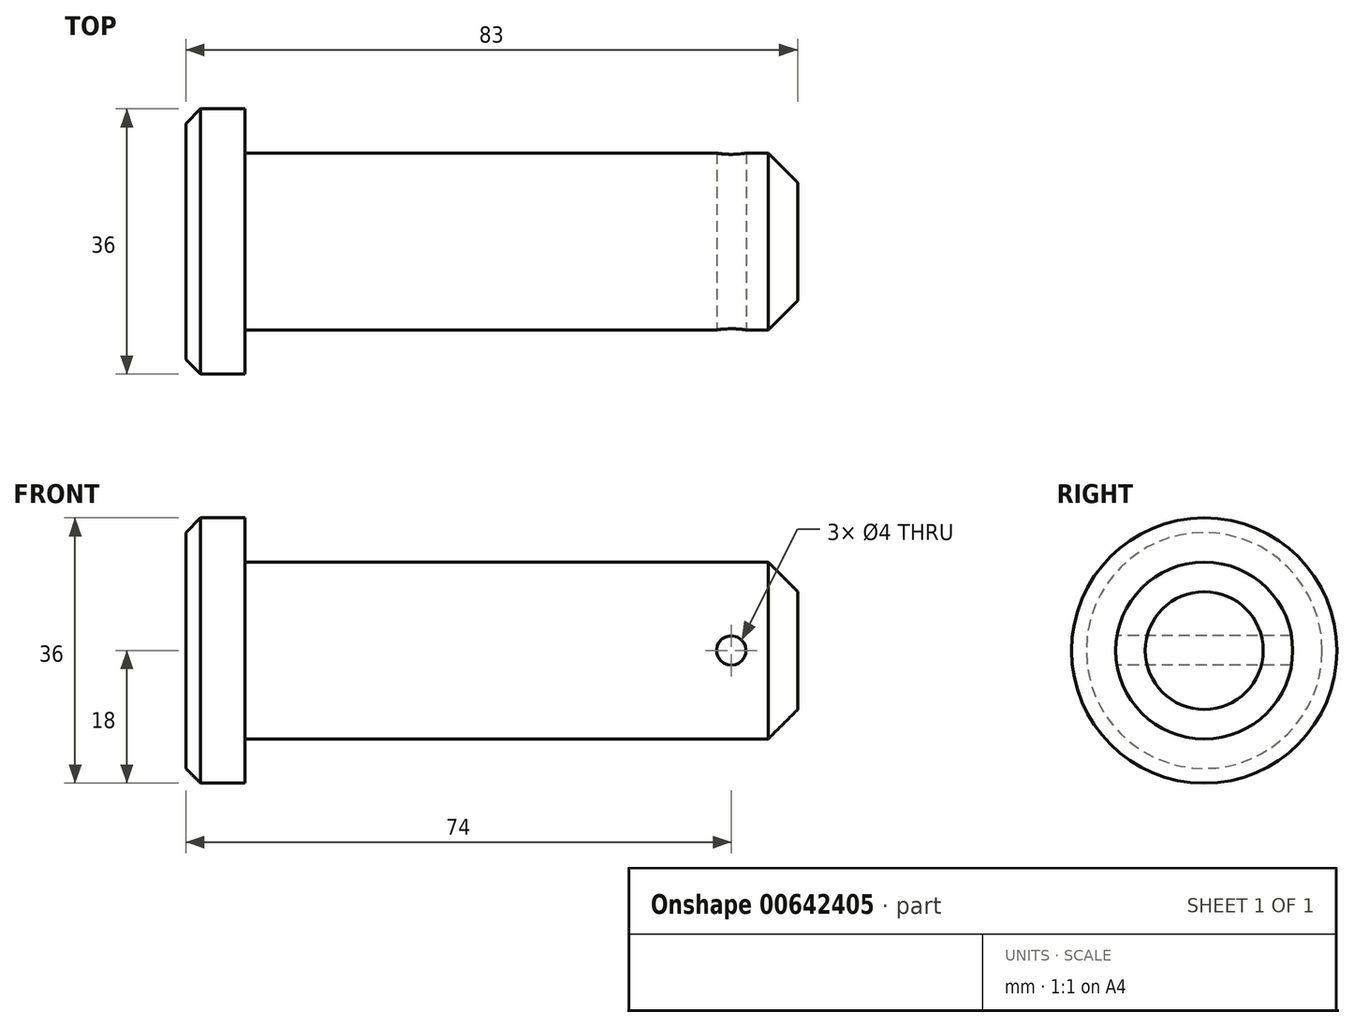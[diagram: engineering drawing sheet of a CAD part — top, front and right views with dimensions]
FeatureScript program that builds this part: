
annotation { "Feature Type Name" : "Feature", "Feature Type Description" : "" }
export const myFeature = defineFeature(function(context is Context, id is Id, definition is map)
    precondition{}
    {
        {
            var Q0;
            Q0=qCreatedBy(makeId("Front.planeOp"),FACE);
            var sketch = newSketch(context, id + "F0", { "sketchPlane" : qUnion([Q0])});
            skLineSegment(sketch, "E0", {"start": v(0, 0) * mm, "end": v(75, 0) * mm, "construction": true});
            skLineSegment(sketch, "E1", {"start": v(0, 12) * mm, "end": v(75, 12) * mm});
            skLineSegment(sketch, "E2", {"start": v(75, 12) * mm, "end": v(75, 0) * mm});
            skLineSegment(sketch, "E3", {"start": v(0, 18) * mm, "end": v(-8, 18) * mm});
            skLineSegment(sketch, "E4", {"start": v(0, 18) * mm, "end": v(0, 12) * mm});
            skLineSegment(sketch, "E5", {"start": v(-8, 18) * mm, "end": v(-8, 0) * mm});
            skLineSegment(sketch, "E6", {"start": v(-8, 0) * mm, "end": v(75, 0) * mm});
            skSolve(sketch);
        }
        {
            var Q0;
            Q0=makeQuery(id+"F0.imprint","IMPRINT",FACE,{"disambiguationData":[TD([[makeQuery(id+"F0.imprint","IMPRINT",EDGE,{"derivedFrom":sQuery(id+"F0.wireOp",EDGE,"E1")}),-1.0]])]});
            var Q1;
            Q1=sQuery(id+"F0.wireOp",EDGE,"E6");
            revolve(context, id + "F1", {"entities" : qUnion([Q0]), "axis" : qUnion([Q1]), "revolveType" : RevolveType.FULL});
        }
        {
            var Q0;
            Q0=makeQuery(id+"F1.opRevolve","SWEPT_EDGE",EDGE,{"disambiguationData":[OSD([sQuery(id+"F0.wireOp",EDGE,"E1"),sQuery(id+"F0.wireOp",EDGE,"E2")])]});
            chamfer(context, id + "F2", {"entities" : qUnion([Q0]), "width" : 4 * mm, "tangentPropagation" : true});
        }
        {
            var Q0;
            Q0=makeQuery(id+"F1.opRevolve","SWEPT_EDGE",EDGE,{"disambiguationData":[OSD([sQuery(id+"F0.wireOp",EDGE,"E3"),sQuery(id+"F0.wireOp",EDGE,"E5")])]});
            chamfer(context, id + "F3", {"entities" : qUnion([Q0]), "width" : 2 * mm, "tangentPropagation" : true});
        }
        {
            var Q0;
            Q0=qCreatedBy(makeId("Front.planeOp"),FACE);
            var sketch = newSketch(context, id + "F4", { "sketchPlane" : qUnion([Q0])});
            skCircle(sketch, "E7", {"center": v(66, 0) * mm, "radius": 2 * mm});
            skSolve(sketch);
        }
        {
            var Q0;
            Q0 = qSketchRegion(id + "F4", true);
            extrude(context, id + "F5", {"entities" : qUnion([Q0]), "operationType" : NewBodyOperationType.REMOVE, "endBound" : BoundingType.SYMMETRIC, "oppositeDirection" : true, "depth" : 25 * mm, "offsetDistance" : 25 * mm});
        }
    });
